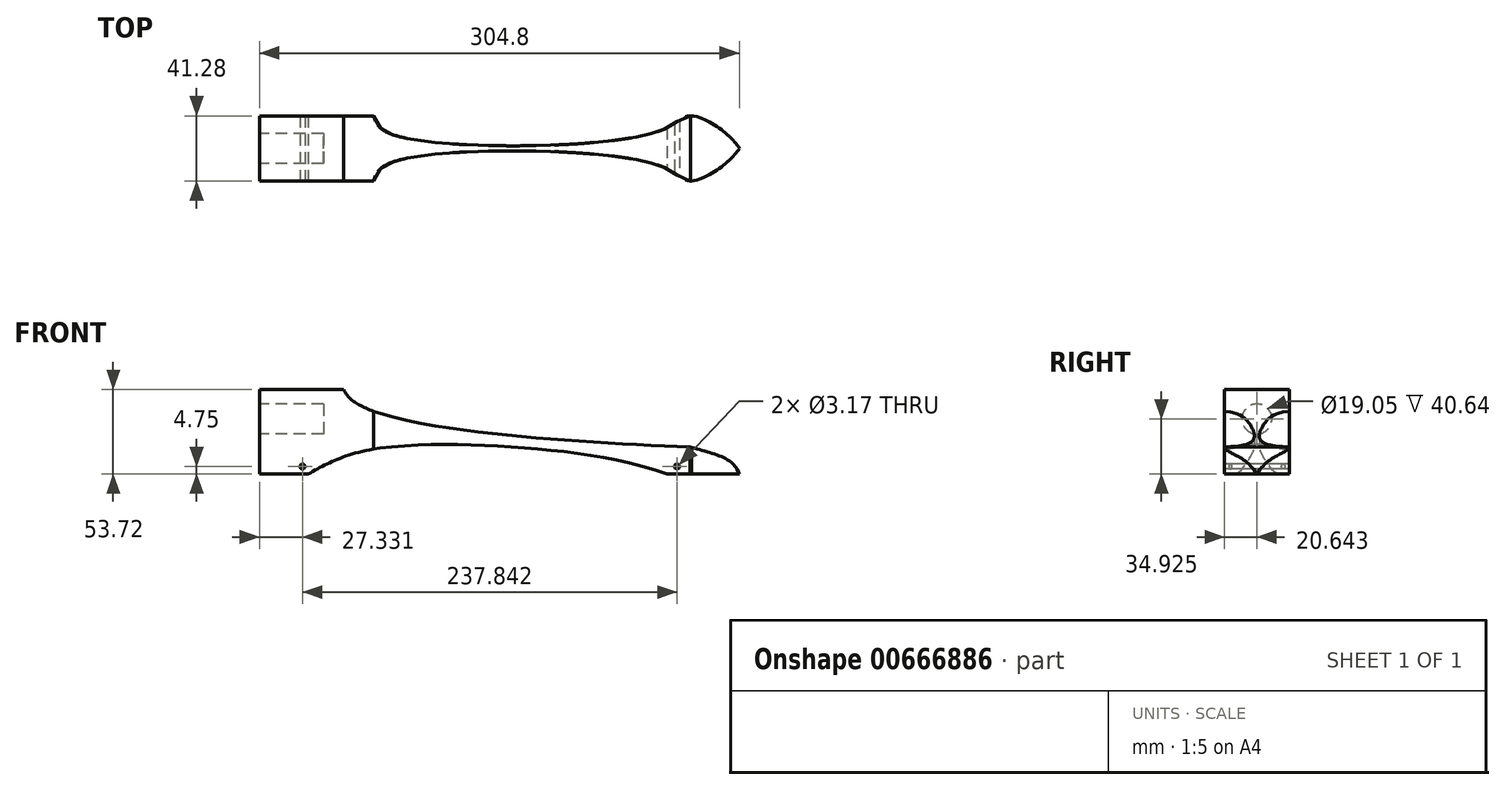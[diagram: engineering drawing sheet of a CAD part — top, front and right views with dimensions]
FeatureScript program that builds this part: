
annotation { "Feature Type Name" : "Feature", "Feature Type Description" : "" }
export const myFeature = defineFeature(function(context is Context, id is Id, definition is map)
    precondition{}
    {
        {
            var Q0;
            Q0=qCreatedBy(makeId("Front.planeOp"),FACE);
            var sketch = newSketch(context, id + "F0", { "sketchPlane" : qUnion([Q0])});
            skLineSegment(sketch, "E0", {"start": v(0, 0) * mm, "end": v(0, 69.85) * mm});
            skLineSegment(sketch, "E1", {"start": v(0, 69.85) * mm, "end": v(304.8, 15.87) * mm});
            skLineSegment(sketch, "E2", {"start": v(304.8, 15.88) * mm, "end": v(304.8, 0) * mm});
            skLineSegment(sketch, "E3", {"start": v(304.8, 0) * mm, "end": v(0, 0) * mm});
            skSolve(sketch);
        }
        {
            var Q0;
            Q0 = qSketchRegion(id + "F0", true);
            extrude(context, id + "F1", {"entities" : qUnion([Q0]), "depth" : 41.27 * mm, "offsetDistance" : 25.4 * mm});
        }
        {
            var Q0;
            Q0=makeQuery(id+"F1.opExtrude","SWEPT_FACE",FACE,{"disambiguationData":[OSD([sQuery(id+"F0.wireOp",EDGE,"E0")])]});
            var sketch = newSketch(context, id + "F2", { "sketchPlane" : qUnion([Q0])});
            skCircle(sketch, "E4", {"center": v(20.64, 34.93) * mm, "radius": 9.53 * mm});
            skPoint(sketch, "E4.centerSnap0", {"position": v(41.28, 34.93) * mm});
            skPoint(sketch, "E4.centerSnap1", {"position": v(20.64, 0) * mm});
            skSolve(sketch);
        }
        {
            var Q0;
            Q0=makeQuery(id+"F1.opExtrude","CAP_FACE",FACE,{"disambiguationData":[OSD([sQuery(id+"F0.wireOp",EDGE,"E0"),sQuery(id+"F0.wireOp",EDGE,"E1"),sQuery(id+"F0.wireOp",EDGE,"E2"),sQuery(id+"F0.wireOp",EDGE,"E3")])],"isStart":false});
            var sketch = newSketch(context, id + "F3", { "sketchPlane" : qUnion([Q0])});
            skLineSegment(sketch, "E5", {"start": v(0, 58.18) * mm, "end": v(0, 69.85) * mm});
            skLineSegment(sketch, "E6", {"start": v(0, 69.85) * mm, "end": v(65.87, 58.18) * mm});
            skLineSegment(sketch, "E7", {"start": v(0, 47.74) * mm, "end": v(0, 53.53) * mm});
            skLineSegment(sketch, "E8", {"start": v(0, 53.53) * mm, "end": v(90.32, 53.86) * mm});
            skSolve(sketch);
        }
        {
            var Q0;
            Q0=makeQuery(id+"F3.imprint","IMPRINT",FACE,{"disambiguationData":[TD([[makeQuery(id+"F3.imprint","IMPRINT",EDGE,{"derivedFrom":sQuery(id+"F3.wireOp",EDGE,"E5")}),-1.0]])]});
            extrude(context, id + "F4", {"entities" : qUnion([Q0]), "operationType" : NewBodyOperationType.REMOVE, "oppositeDirection" : true, "depth" : 50.8 * mm, "offsetDistance" : 25.4 * mm});
        }
        {
            var Q0;
            Q0=makeQuery(id+"F1.opExtrude","CAP_FACE",FACE,{"disambiguationData":[OSD([sQuery(id+"F0.wireOp",EDGE,"E0"),sQuery(id+"F0.wireOp",EDGE,"E1"),sQuery(id+"F0.wireOp",EDGE,"E2"),sQuery(id+"F0.wireOp",EDGE,"E3")])],"isStart":false});
            var sketch = newSketch(context, id + "F5", { "sketchPlane" : qUnion([Q0])});
            skFitSpline(sketch, "E9", {"points": [v(53.54, 53.72) * mm, v(81.14, 37.1) * mm, v(304.8, 15.88) * mm], "startDerivative": vector(32.12, -82.1) * mm, "endDerivative": vector(438.2, -14.7) * mm});
            skSolve(sketch);
        }
        {
            var Q0;
            Q0 = qSketchRegion(id + "F5", true);
            var Q1;
            {var subQ0=sQuery(id+"F5.wireOp",EDGE,"E9");Q1=makeQuery(id+"F5.imprint","IMPRINT",FACE,{"disambiguationData":[TD([[makeQuery(id+"F5.imprint","IMPRINT",EDGE,{"derivedFrom":subQ0}),1.0]])]});}
            extrude(context, id + "F6", {"entities" : qUnion([Q0, Q1]), "operationType" : NewBodyOperationType.REMOVE, "oppositeDirection" : true, "depth" : 50.8 * mm, "offsetDistance" : 25.4 * mm});
        }
        {
            var Q0;
            Q0=makeQuery(id+"F1.opExtrude","SWEPT_FACE",FACE,{"disambiguationData":[OSD([sQuery(id+"F0.wireOp",EDGE,"E0")])]});
            var sketch = newSketch(context, id + "F7", { "sketchPlane" : qUnion([Q0])});
            skSolve(sketch);
        }
        {
            var Q0;
            Q0=makeQuery(id+"F2.imprint","IMPRINT",FACE,{"disambiguationData":[TD([[makeQuery(id+"F2.imprint","IMPRINT",EDGE,{"derivedFrom":sQuery(id+"F2.wireOp",EDGE,"E4")}),1.0]])]});
            extrude(context, id + "F8", {"entities" : qUnion([Q0]), "operationType" : NewBodyOperationType.REMOVE, "oppositeDirection" : true, "depth" : 40.64 * mm, "offsetDistance" : 25.4 * mm});
        }
        {
            var Q0;
            Q0=makeQuery(id+"F1.opExtrude","CAP_FACE",FACE,{"disambiguationData":[OSD([sQuery(id+"F0.wireOp",EDGE,"E0"),sQuery(id+"F0.wireOp",EDGE,"E1"),sQuery(id+"F0.wireOp",EDGE,"E2"),sQuery(id+"F0.wireOp",EDGE,"E3")])],"isStart":false});
            var sketch = newSketch(context, id + "F9", { "sketchPlane" : qUnion([Q0])});
            skFitSpline(sketch, "E10", {"points": [v(30.96, 0) * mm, v(74.38, 16.06) * mm, v(210.63, 11.86) * mm, v(258.84, 0) * mm], "startDerivative": vector(127.48, 72.25) * mm, "endDerivative": vector(140.02, -45.46) * mm});
            skSolve(sketch);
        }
        {
            var Q0;
            Q0 = qSketchRegion(id + "F9", true);
            var Q1;
            {var subQ0=sQuery(id+"F9.wireOp",EDGE,"E10");Q1=makeQuery(id+"F9.imprint","IMPRINT",FACE,{"disambiguationData":[TD([[makeQuery(id+"F9.imprint","IMPRINT",EDGE,{"derivedFrom":subQ0}),-1.0]])]});}
            extrude(context, id + "F10", {"entities" : qUnion([Q0, Q1]), "operationType" : NewBodyOperationType.REMOVE, "oppositeDirection" : true, "depth" : 76.2 * mm, "offsetDistance" : 25.4 * mm});
        }
        {
            var Q0;
            Q0=makeQuery(id+"F1.opExtrude","CAP_FACE",FACE,{"disambiguationData":[OSD([sQuery(id+"F0.wireOp",EDGE,"E0"),sQuery(id+"F0.wireOp",EDGE,"E1"),sQuery(id+"F0.wireOp",EDGE,"E2"),sQuery(id+"F0.wireOp",EDGE,"E3")])],"isStart":false});
            var sketch = newSketch(context, id + "F11", { "sketchPlane" : qUnion([Q0])});
            skPoint(sketch, "E11.1.internal.snap0", {"position": v(304.8, 7.94) * mm});
            skFitSpline(sketch, "E11", {"points": [v(273.73, 17.04) * mm, v(298.9, 7.94) * mm, v(304.8, 0) * mm], "startDerivative": vector(48.2, -12.73) * mm, "endDerivative": vector(10.9, -22.2) * mm});
            skSolve(sketch);
        }
        {
            var Q0;
            Q0 = qSketchRegion(id + "F11", true);
            var Q1;
            {var subQ0=sQuery(id+"F11.wireOp",EDGE,"E11");Q1=makeQuery(id+"F11.imprint","IMPRINT",FACE,{"disambiguationData":[TD([[makeQuery(id+"F11.imprint","IMPRINT",EDGE,{"derivedFrom":subQ0}),1.0]])]});}
            extrude(context, id + "F12", {"entities" : qUnion([Q0, Q1]), "operationType" : NewBodyOperationType.REMOVE, "oppositeDirection" : true, "depth" : 76.2 * mm, "offsetDistance" : 25.4 * mm});
        }
        {
            var Q0;
            Q0=makeQuery(id+"F1.opExtrude","CAP_FACE",FACE,{"disambiguationData":[OSD([sQuery(id+"F0.wireOp",EDGE,"E0"),sQuery(id+"F0.wireOp",EDGE,"E1"),sQuery(id+"F0.wireOp",EDGE,"E2"),sQuery(id+"F0.wireOp",EDGE,"E3")])],"isStart":false});
            var sketch = newSketch(context, id + "F13", { "sketchPlane" : qUnion([Q0])});
            skLineSegment(sketch, "E12", {"start": v(-12.47, 0) * mm, "end": v(-12.47, 4.75) * mm});
            skCircle(sketch, "E13", {"center": v(27.33, 4.75) * mm, "radius": 1.59 * mm});
            skCircle(sketch, "E14", {"center": v(265.17, 4.75) * mm, "radius": 1.59 * mm});
            skSolve(sketch);
        }
        {
            var Q0;
            Q0 = qSketchRegion(id + "F13", true);
            extrude(context, id + "F14", {"entities" : qUnion([Q0]), "operationType" : NewBodyOperationType.REMOVE, "oppositeDirection" : true, "depth" : 76.2 * mm, "offsetDistance" : 25.4 * mm});
        }
        {
            var Q0;
            Q0=qCreatedBy(makeId("Top.planeOp"),FACE);
            cPlane(context, id + "F15", {"entities" : qUnion([Q0]), "cplaneType" : CPlaneType.OFFSET, "offset" : 53.34 * mm, "width" : 152.4 * mm, "height" : 152.4 * mm});
        }
        {
            var Q0;
            Q0=qCreatedBy(id+"F15.planeOp",FACE);
            var sketch = newSketch(context, id + "F16", { "sketchPlane" : qUnion([Q0])});
            skFitSpline(sketch, "E15", {"points": [v(72.46, 0) * mm, v(86.1, -12.44) * mm, v(254.2, -9.65) * mm, v(274.22, 0) * mm, v(304.8, -20.64) * mm], "startDerivative": vector(25.65, -96.68) * mm, "endDerivative": vector(93.28, -143.54) * mm});
            skPoint(sketch, "E16.0", {"position": v(304.8, 0) * mm});
            skPoint(sketch, "E17.0", {"position": v(304.8, -41.28) * mm});
            skPoint(sketch, "E18.0", {"position": v(0, -41.28) * mm});
            skPoint(sketch, "E19.0", {"position": v(0, -20.64) * mm});
            skLineSegment(sketch, "E20.0", {"start": v(0, 0) * mm, "end": v(53.54, 0) * mm});
            skLineSegment(sketch, "E21", {"start": v(0, -20.64) * mm, "end": v(304.8, -20.64) * mm});
            skFitSpline(sketch, "E22.MirrorCS", {"points": [v(72.46, -41.27) * mm, v(86.1, -28.83) * mm, v(254.2, -31.63) * mm, v(274.22, -41.28) * mm, v(304.8, -20.64) * mm], "startDerivative": vector(25.65, 96.68) * mm, "endDerivative": vector(93.28, 143.54) * mm});
            skLineSegment(sketch, "E23", {"start": v(72.46, 0) * mm, "end": v(274.22, 0) * mm});
            skLineSegment(sketch, "E24", {"start": v(72.46, -41.27) * mm, "end": v(274.22, -41.27) * mm});
            skLineSegment(sketch, "E25", {"start": v(274.22, 0) * mm, "end": v(304.8, 0) * mm});
            skLineSegment(sketch, "E26", {"start": v(304.8, -20.64) * mm, "end": v(304.8, 0) * mm});
            skLineSegment(sketch, "E27", {"start": v(274.22, -41.28) * mm, "end": v(304.8, -41.27) * mm});
            skLineSegment(sketch, "E28", {"start": v(304.8, -20.64) * mm, "end": v(304.8, -41.27) * mm});
            skSolve(sketch);
        }
        {
            var Q0;
            {var subQ0=sQuery(id+"F16.wireOp",EDGE,"E24");var subQ1=sQuery(id+"F16.wireOp",EDGE,"E22.MirrorCS");var subQ2=makeQuery(id+"F16.imprint","INTERSECT",VERTEX,{"disambiguationData":[OD(0.0)],"derivedFrom":[subQ1,subQ0]});Q0=makeQuery(id+"F16.imprint","IMPRINT",FACE,{"disambiguationData":[TD([[makeQuery(id+"F16.imprint","IMPRINT",EDGE,{"disambiguationData":[TD([[subQ2,-1.0]])],"derivedFrom":subQ1}),-1.0]])]});}
            var Q1;
            {var subQ0=sQuery(id+"F16.wireOp",EDGE,"E23");var subQ1=sQuery(id+"F16.wireOp",EDGE,"E15");var subQ2=makeQuery(id+"F16.imprint","INTERSECT",VERTEX,{"disambiguationData":[OD(0.0)],"derivedFrom":[subQ1,subQ0]});Q1=makeQuery(id+"F16.imprint","IMPRINT",FACE,{"disambiguationData":[TD([[makeQuery(id+"F16.imprint","IMPRINT",EDGE,{"disambiguationData":[TD([[subQ2,-1.0]])],"derivedFrom":subQ1}),1.0]])]});}
            var Q2;
            {var subQ2=sQuery(id+"F16.wireOp",EDGE,"E25");Q2=makeQuery(id+"F16.imprint","IMPRINT",FACE,{"disambiguationData":[TD([[makeQuery(id+"F16.imprint","IMPRINT",EDGE,{"derivedFrom":subQ2}),-1.0]])]});}
            var Q3;
            {var subQ2=sQuery(id+"F16.wireOp",EDGE,"E27");Q3=makeQuery(id+"F16.imprint","IMPRINT",FACE,{"disambiguationData":[TD([[makeQuery(id+"F16.imprint","IMPRINT",EDGE,{"derivedFrom":subQ2}),1.0]])]});}
            extrude(context, id + "F17", {"entities" : qUnion([Q0, Q1, Q2, Q3]), "operationType" : NewBodyOperationType.REMOVE, "oppositeDirection" : true, "depth" : 62.23 * mm, "offsetDistance" : 25.4 * mm});
        }
    });
